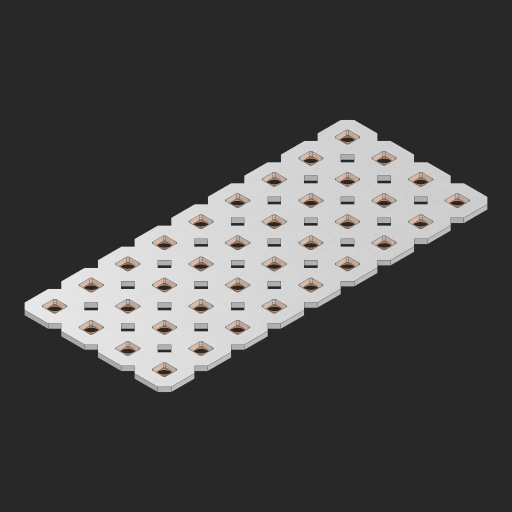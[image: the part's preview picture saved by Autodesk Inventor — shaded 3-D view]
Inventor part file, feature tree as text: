
AUTODESK INVENTOR PART (.ipt)
format: ipt  version: 2023 (Build 270158000, 158)  size: 714,752 bytes
history: native  units: in
note: dims shown in document units (in); Inventor stores cm internally (conversion verified against a paired STEP export)
features: other x37, extrude x35, sketch x2, pattern_linear x1
ambient origin geometry x8: Origin, YZ Plane, XZ Plane, XY Plane, X Axis, Y Axis, Z Axis, Center Point
bodies: Solid1 (feature_tree), Body (feature_tree)
feature tree (75):
  pattern_linear  "Rectangular Pattern1"  Spacing1=0.09in  [1 undecoded]
  sketch  "Sketch1"  dims[d1=0.5in]
  sketch  "Sketch2"  dims[d2=0.182in d3=0.09in d4=0.09in d5=0.09in d6=0.09in d7=0.09in d8=0.09in d9=0.09in d10=0.09in d11=0.02in d13=0.0in d14=0.172in d15=0.0625in d16=0.0in d19=0.5in d22=0.5in]
  other  "Srf1"
  other  "Srf126"
  other  "Srf127"
  other  "Srf128"
  other  "Srf129"
  other  "Srf130"
  other  "Srf131"
  other  "Srf250"
  other  "Srf251"
  other  "Srf268"
  other  "Srf269"
  other  "Srf270"
  other  "Srf271"
  other  "Srf272"
  other  "Srf273"
  other  "Srf274"
  other  "Srf275"
  other  "Srf276"
  other  "Srf293"
  other  "Srf294"
  other  "Srf295"
  other  "Srf296"
  other  "Srf297"
  other  "Srf298"
  other  "Srf299"
  other  "Srf300"
  other  "Srf301"
  other  "Srf318"
  other  "Srf319"
  other  "Srf320"
  other  "Srf321"
  other  "Srf322"
  other  "Srf323"
  other  "Srf324"
  other  "Srf325"
  other  "Srf326"
  other  "Circle"
  extrude  "ExtrusionSrf126"  Depth=0.09in
  extrude  "ExtrusionSrf127"  Depth=0.09in
  extrude  "ExtrusionSrf128"  Depth=0.09in
  extrude  "ExtrusionSrf129"  Depth=0.09in
  extrude  "ExtrusionSrf130"  Depth=0.09in
  extrude  "ExtrusionSrf131"  Depth=0.09in
  extrude  "ExtrusionSrf250"  Depth=0.09in
  extrude  "ExtrusionSrf251"  Depth=0.02in
  extrude  "ExtrusionSrf268"  TaperAngle=0.0deg  [1 undecoded]
  extrude  "ExtrusionSrf269"  Depth=0.5in
  extrude  "ExtrusionSrf270"  Depth=0.0625in TaperAngle=0.0deg
  extrude  "ExtrusionSrf271"  Depth=0.5in
  extrude  "ExtrusionSrf272"  Depth=0.5in
  extrude  "ExtrusionSrf273"  [1 undecoded]
  extrude  "ExtrusionSrf274"  [1 undecoded]
  extrude  "ExtrusionSrf275"  [1 undecoded]
  extrude  "ExtrusionSrf276"  [1 undecoded]
  extrude  "ExtrusionSrf293"  [1 undecoded]
  extrude  "ExtrusionSrf294"  [1 undecoded]
  extrude  "ExtrusionSrf295"  [1 undecoded]
  extrude  "ExtrusionSrf296"  [1 undecoded]
  extrude  "ExtrusionSrf297"  [1 undecoded]
  extrude  "ExtrusionSrf298"  [1 undecoded]
  extrude  "ExtrusionSrf299"  [1 undecoded]
  extrude  "ExtrusionSrf300"  [1 undecoded]
  extrude  "ExtrusionSrf301"  [1 undecoded]
  extrude  "ExtrusionSrf318"  [1 undecoded]
  extrude  "ExtrusionSrf319"  [1 undecoded]
  extrude  "ExtrusionSrf320"  [1 undecoded]
  extrude  "ExtrusionSrf321"  [1 undecoded]
  extrude  "ExtrusionSrf322"  [1 undecoded]
  extrude  "ExtrusionSrf323"  [1 undecoded]
  extrude  "ExtrusionSrf324"  [1 undecoded]
  extrude  "ExtrusionSrf325"  [1 undecoded]
  extrude  "ExtrusionSrf326"  [1 undecoded]
note: 24 required parameter values undecoded (feature->parameter linkage not recoverable at this tier; creation-order binding heuristic only, values carry confidence <= 0.55)
